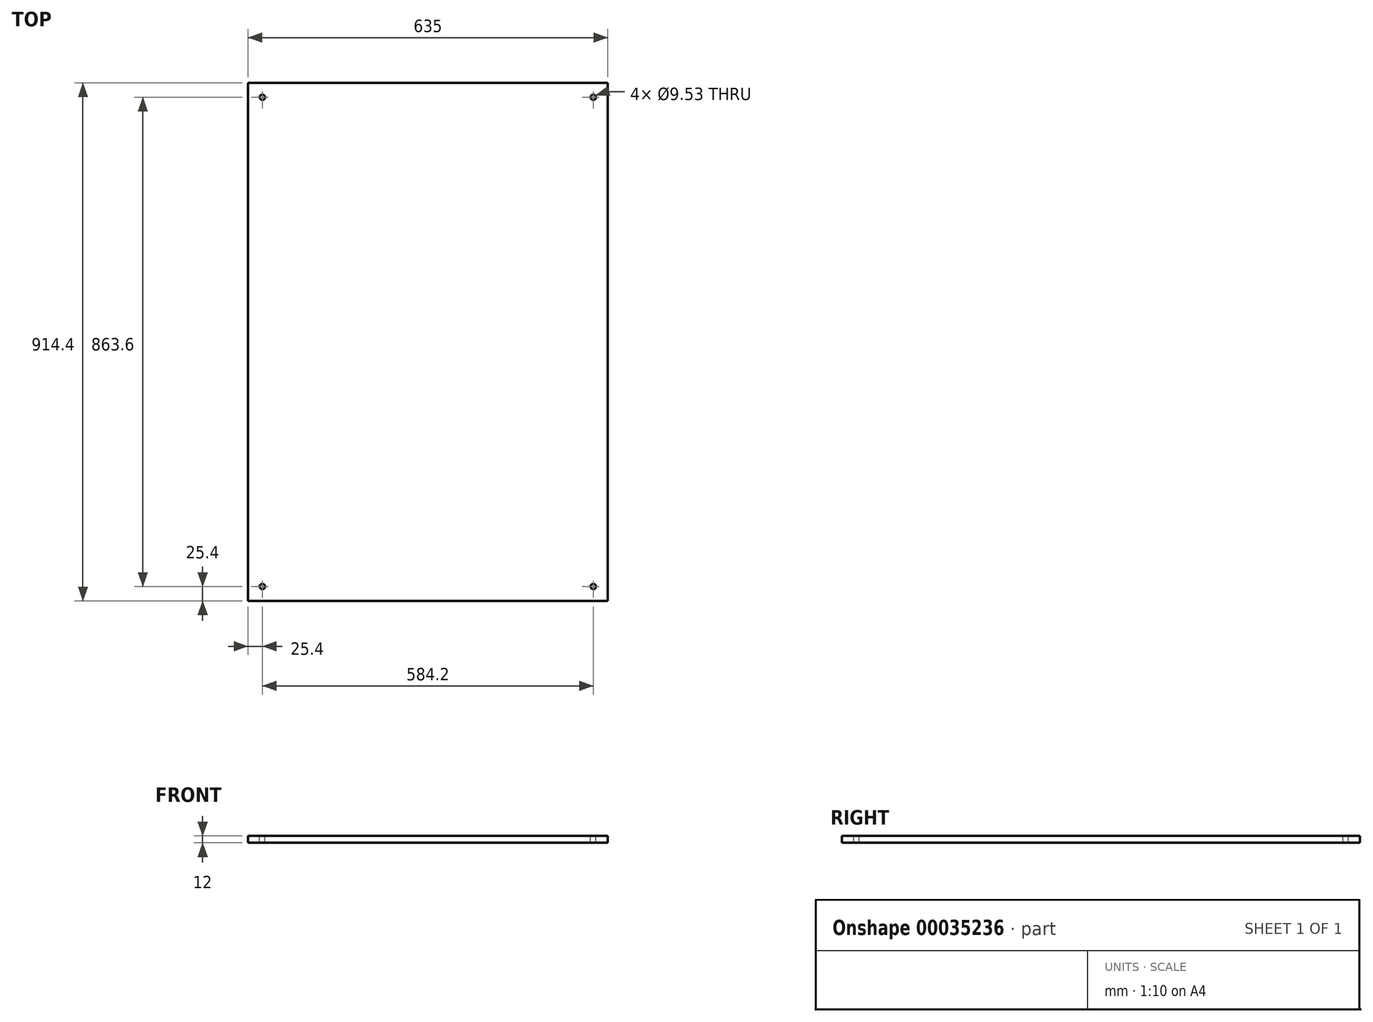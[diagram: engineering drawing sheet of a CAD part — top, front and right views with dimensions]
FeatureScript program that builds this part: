
annotation { "Feature Type Name" : "Feature", "Feature Type Description" : "" }
export const myFeature = defineFeature(function(context is Context, id is Id, definition is map)
    precondition{}
    {
        {
            var Q0;
            Q0=qCreatedBy(makeId("Top.planeOp"),FACE);
            var sketch = newSketch(context, id + "F0", { "sketchPlane" : qUnion([Q0])});
            skLineSegment(sketch, "E0.rect.bottom", {"start": v(305.5, -445.2) * mm, "end": v(-305.5, -445.2) * mm});
            skLineSegment(sketch, "E0.rect.top", {"start": v(305.5, 445.2) * mm, "end": v(-305.5, 445.2) * mm});
            skLineSegment(sketch, "E0.rect.left", {"start": v(305.5, -445.2) * mm, "end": v(305.5, 445.2) * mm});
            skLineSegment(sketch, "E0.rect.right", {"start": v(-305.5, -445.2) * mm, "end": v(-305.5, 445.2) * mm});
            skPoint(sketch, "E0.rect.middle", {"position": v(0, 0) * mm});
            skLineSegment(sketch, "E1.rect.bottom", {"start": v(317.5, -457.2) * mm, "end": v(-317.5, -457.2) * mm});
            skLineSegment(sketch, "E1.rect.top", {"start": v(317.5, 457.2) * mm, "end": v(-317.5, 457.2) * mm});
            skLineSegment(sketch, "E1.rect.left", {"start": v(317.5, -457.2) * mm, "end": v(317.5, 457.2) * mm});
            skLineSegment(sketch, "E1.rect.right", {"start": v(-317.5, -457.2) * mm, "end": v(-317.5, 457.2) * mm});
            skSolve(sketch);
        }
        {
            var Q0;
            Q0 = qSketchRegion(id + "F0", true);
            var Q1;
            Q1=makeQuery(id+"F0.imprint","IMPRINT",FACE,{"disambiguationData":[TD([[makeQuery(id+"F0.imprint","IMPRINT",EDGE,{"derivedFrom":sQuery(id+"F0.wireOp",EDGE,"E0.rect.bottom")}),-1.0]])]});
            extrude(context, id + "F1", {"entities" : qUnion([Q0, Q1]), "endBound" : BoundingType.SYMMETRIC, "oppositeDirection" : true, "depth" : 12 * mm});
        }
        {
            var Q0;
            Q0=makeQuery(id+"F1.opExtrude","CAP_FACE",FACE,{"disambiguationData":[OSD([sQuery(id+"F0.wireOp",EDGE,"E1.rect.bottom"),sQuery(id+"F0.wireOp",EDGE,"E1.rect.top"),sQuery(id+"F0.wireOp",EDGE,"E1.rect.left"),sQuery(id+"F0.wireOp",EDGE,"E1.rect.right")])],"isStart":true});
            var sketch = newSketch(context, id + "F2", { "sketchPlane" : qUnion([Q0])});
            skLineSegment(sketch, "E2.rect.bottom", {"start": v(-292.1, 431.8) * mm, "end": v(292.1, 431.8) * mm, "construction": true});
            skLineSegment(sketch, "E2.rect.top", {"start": v(-292.1, -431.8) * mm, "end": v(292.1, -431.8) * mm, "construction": true});
            skLineSegment(sketch, "E2.rect.left", {"start": v(-292.1, 431.8) * mm, "end": v(-292.1, -431.8) * mm, "construction": true});
            skLineSegment(sketch, "E2.rect.right", {"start": v(292.1, 431.8) * mm, "end": v(292.1, -431.8) * mm, "construction": true});
            skPoint(sketch, "E2.rect.middle", {"position": v(0, 0) * mm});
            skCircle(sketch, "E3", {"center": v(-292.1, 431.8) * mm, "radius": 4.76 * mm});
            skCircle(sketch, "E4", {"center": v(292.1, 431.8) * mm, "radius": 4.76 * mm});
            skCircle(sketch, "E5", {"center": v(-292.1, -431.8) * mm, "radius": 4.76 * mm});
            skCircle(sketch, "E6", {"center": v(292.1, -431.8) * mm, "radius": 4.76 * mm});
            skSolve(sketch);
        }
        {
            var Q0;
            Q0 = qSketchRegion(id + "F2", true);
            extrude(context, id + "F3", {"entities" : qUnion([Q0]), "operationType" : NewBodyOperationType.REMOVE, "oppositeDirection" : true, "depth" : 25.4 * mm});
        }
    });
